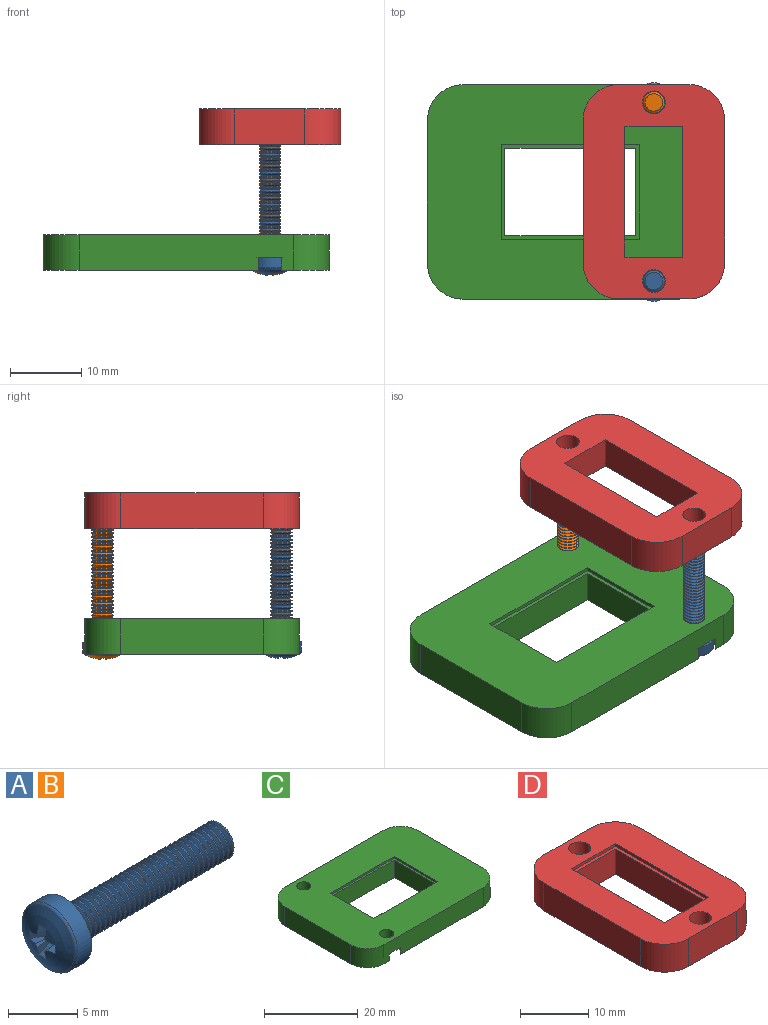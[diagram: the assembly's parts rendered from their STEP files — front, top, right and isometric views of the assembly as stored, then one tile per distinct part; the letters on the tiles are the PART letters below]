
ASSEMBLY  parts=4 mates=3
PART A: 127 faces, bbox 18.4x6.1x6.1 mm
  f0: sphere r=5mm, area 20.9mm2, adj f1,f2,f3,f4,f5,f6,f15,f16
  f1: plane 1.72x0.9mm, normal (0,-1,0), area 0.7mm2, adj f0,f5,f12,f32
  f2: plane 1.72x0.9mm, normal (0,-1,0), area 0.7mm2, adj f0,f6,f9,f33
  f3: plane 1.72x0.9mm, normal (0,1,0), area 0.7mm2, adj f0,f5,f13,f28
  f4: plane 1.72x0.9mm, normal (0,1,0), area 0.7mm2, adj f0,f6,f8,f31
  f5: plane 1.57x0.79mm, normal (-0.45,0,-0.89), area 1.3mm2, adj f0,f1,f3,f12,f13,f26
  f6: plane 1.57x0.79mm, normal (-0.45,0,0.89), area 1.3mm2, adj f0,f2,f4,f8,f9,f27
  f7: plane 0.19x0.11mm, normal (-1,0,0), area 0mm2, adj f16,f17,f34
  f8: plane 0.19x0.11mm, normal (-1,0,0), area 0mm2, adj f4,f6,f34
  f9: plane 0.19x0.11mm, normal (-1,0,0), area 0mm2, adj f2,f6,f34
  f10: plane 0.19x0.11mm, normal (-1,0,0), area 0mm2, adj f18,f20,f34
  f11: plane 0.19x0.11mm, normal (-1,0,0), area 0mm2, adj f18,f19,f34
  f12: plane 0.19x0.11mm, normal (-1,0,0), area 0mm2, adj f1,f5,f34
  f13: plane 0.19x0.11mm, normal (-1,0,0), area 0mm2, adj f3,f5,f34
  f14: plane 0.19x0.11mm, normal (-1,0,0), area 0mm2, adj f15,f17,f34
  f15: plane 1.72x0.9mm, normal (0,0,-1), area 0.7mm2, adj f0,f14,f17,f28
  f16: plane 1.72x0.9mm, normal (0,0,1), area 0.7mm2, adj f0,f7,f17,f31
  f17: plane 1.6x0.81mm, normal (-0.45,0.89,0), area 1.3mm2, adj f0,f7,f14,f15,f16,f29
  f18: plane 1.57x0.79mm, normal (-0.45,-0.89,0), area 1.3mm2, adj f0,f10,f11,f19,f20,f30
  f19: plane 1.72x0.9mm, normal (0,0,-1), area 0.7mm2, adj f0,f11,f18,f32
  f20: plane 1.72x0.9mm, normal (0,0,1), area 0.7mm2, adj f0,f10,f18,f33
  f21: cylinder r=1.5mm len=3mm, axis (-1,0,0), area 6.6mm2, adj f25,f36
  f22: plane 5.6x5.6mm, normal (1,0,0), area 16.6mm2, adj f23,f25
  f23: cylinder r=2.8mm len=5.6mm, axis (-1,0,0), area 24.6mm2, adj f22,f24
  f24: torus R=2.53mm, axis (-1,0,0), area 4.7mm2, adj f0,f23
  f25: torus R=1.6mm, axis (-1,0,0), area 1.5mm2, adj f21,f22
  f26: cone r=0.56mm half-angle=4deg, axis (-1,0,0), area 0mm2, adj f5,f34
  f27: cone r=0.56mm half-angle=4deg, axis (-1,0,0), area 0mm2, adj f6,f34
  f28: cone r=0.56mm half-angle=4deg, axis (-1,0,0), area 0.3mm2, adj f0,f3,f15,f34
  f29: cone r=0.56mm half-angle=4deg, axis (-1,0,0), area 0mm2, adj f17,f34
  f30: cone r=0.56mm half-angle=4deg, axis (-1,0,0), area 0mm2, adj f18,f34
  f31: cone r=0.56mm half-angle=4deg, axis (-1,0,0), area 0.3mm2, adj f0,f4,f16,f34
  f32: cone r=0.56mm half-angle=4deg, axis (-1,0,0), area 0.3mm2, adj f0,f1,f19,f34
  f33: cone r=0.56mm half-angle=4deg, axis (-1,0,0), area 0.3mm2, adj f0,f2,f20,f34
  f34: cone r=0mm half-angle=72deg, axis (-1,0,0), area 1mm2, adj f7,f8,f9,f10,f11,f12,f13,f14
  f35: cone r=1.5mm half-angle=55deg, axis (1,0,0), area 2.9mm2, adj f36,f37
  f36: cone r=1.22mm half-angle=55deg, axis (-1,0,0), area 2.9mm2, adj f21,f35
  f37: cylinder r=1.5mm len=3mm, axis (-1,0,0), area 1mm2, adj f35,f39
  f38: cone r=1.5mm half-angle=55deg, axis (1,0,0), area 2.9mm2, adj f39,f40
  f39: cone r=1.22mm half-angle=55deg, axis (-1,0,0), area 2.9mm2, adj f37,f38
  f40: cylinder r=1.5mm len=3mm, axis (-1,0,0), area 1mm2, adj f38,f42
  f41: cone r=1.5mm half-angle=55deg, axis (1,0,0), area 2.9mm2, adj f42,f43
  f42: cone r=1.22mm half-angle=55deg, axis (-1,0,0), area 2.9mm2, adj f40,f41
  f43: cylinder r=1.5mm len=3mm, axis (-1,0,0), area 1mm2, adj f41,f45
  f44: cone r=1.5mm half-angle=55deg, axis (1,0,0), area 2.9mm2, adj f45,f46
  f45: cone r=1.22mm half-angle=55deg, axis (-1,0,0), area 2.9mm2, adj f43,f44
  f46: cylinder r=1.5mm len=3mm, axis (-1,0,0), area 1mm2, adj f44,f48
  f47: cone r=1.5mm half-angle=55deg, axis (1,0,0), area 2.9mm2, adj f48,f49
  f48: cone r=1.22mm half-angle=55deg, axis (-1,0,0), area 2.9mm2, adj f46,f47
  f49: cylinder r=1.5mm len=3mm, axis (-1,0,0), area 1mm2, adj f47,f51
  f50: cone r=1.5mm half-angle=55deg, axis (1,0,0), area 2.9mm2, adj f51,f52
  f51: cone r=1.22mm half-angle=55deg, axis (-1,0,0), area 2.9mm2, adj f49,f50
  f52: cylinder r=1.5mm len=3mm, axis (-1,0,0), area 1mm2, adj f50,f54
  f53: cone r=1.5mm half-angle=55deg, axis (1,0,0), area 2.9mm2, adj f54,f55
  f54: cone r=1.22mm half-angle=55deg, axis (-1,0,0), area 2.9mm2, adj f52,f53
  f55: cylinder r=1.5mm len=3mm, axis (-1,0,0), area 1mm2, adj f53,f57
  f56: cone r=1.5mm half-angle=55deg, axis (1,0,0), area 2.9mm2, adj f57,f58
  f57: cone r=1.22mm half-angle=55deg, axis (-1,0,0), area 2.9mm2, adj f55,f56
  f58: cylinder r=1.5mm len=3mm, axis (-1,0,0), area 1mm2, adj f56,f60
  f59: cone r=1.5mm half-angle=55deg, axis (1,0,0), area 2.9mm2, adj f60,f61
  f60: cone r=1.22mm half-angle=55deg, axis (-1,0,0), area 2.9mm2, adj f58,f59
  f61: cylinder r=1.5mm len=3mm, axis (-1,0,0), area 1mm2, adj f59,f63
  f62: cone r=1.5mm half-angle=55deg, axis (1,0,0), area 2.9mm2, adj f63,f64
  f63: cone r=1.22mm half-angle=55deg, axis (-1,0,0), area 2.9mm2, adj f61,f62
  f64: cylinder r=1.5mm len=3mm, axis (-1,0,0), area 1mm2, adj f62,f66
  f65: cone r=1.5mm half-angle=55deg, axis (1,0,0), area 2.9mm2, adj f66,f67
  f66: cone r=1.22mm half-angle=55deg, axis (-1,0,0), area 2.9mm2, adj f64,f65
  f67: cylinder r=1.5mm len=3mm, axis (-1,0,0), area 1mm2, adj f65,f69
  f68: cone r=1.5mm half-angle=55deg, axis (1,0,0), area 2.9mm2, adj f69,f70
  f69: cone r=1.22mm half-angle=55deg, axis (-1,0,0), area 2.9mm2, adj f67,f68
  f70: cylinder r=1.5mm len=3mm, axis (-1,0,0), area 1mm2, adj f68,f72
  f71: cone r=1.5mm half-angle=55deg, axis (1,0,0), area 2.9mm2, adj f72,f73
  f72: cone r=1.22mm half-angle=55deg, axis (-1,0,0), area 2.9mm2, adj f70,f71
  f73: cylinder r=1.5mm len=3mm, axis (-1,0,0), area 1mm2, adj f71,f75
  f74: cone r=1.5mm half-angle=55deg, axis (1,0,0), area 2.9mm2, adj f75,f76
  f75: cone r=1.22mm half-angle=55deg, axis (-1,0,0), area 2.9mm2, adj f73,f74
  f76: cylinder r=1.5mm len=3mm, axis (-1,0,0), area 1mm2, adj f74,f78
  f77: cone r=1.5mm half-angle=55deg, axis (1,0,0), area 2.9mm2, adj f78,f79
  f78: cone r=1.22mm half-angle=55deg, axis (-1,0,0), area 2.9mm2, adj f76,f77
  f79: cylinder r=1.5mm len=3mm, axis (-1,0,0), area 1mm2, adj f77,f81
  f80: cone r=1.5mm half-angle=55deg, axis (1,0,0), area 2.9mm2, adj f81,f82
  f81: cone r=1.22mm half-angle=55deg, axis (-1,0,0), area 2.9mm2, adj f79,f80
  f82: cylinder r=1.5mm len=3mm, axis (-1,0,0), area 1mm2, adj f80,f84
  f83: cone r=1.5mm half-angle=55deg, axis (1,0,0), area 2.9mm2, adj f84,f85
  f84: cone r=1.22mm half-angle=55deg, axis (-1,0,0), area 2.9mm2, adj f82,f83
  f85: cylinder r=1.5mm len=3mm, axis (-1,0,0), area 1mm2, adj f83,f87
  f86: cone r=1.5mm half-angle=55deg, axis (1,0,0), area 2.9mm2, adj f87,f88
  f87: cone r=1.22mm half-angle=55deg, axis (-1,0,0), area 2.9mm2, adj f85,f86
  f88: cylinder r=1.5mm len=3mm, axis (-1,0,0), area 1mm2, adj f86,f90
  f89: cone r=1.5mm half-angle=55deg, axis (1,0,0), area 2.9mm2, adj f90,f91
  f90: cone r=1.22mm half-angle=55deg, axis (-1,0,0), area 2.9mm2, adj f88,f89
  f91: cylinder r=1.5mm len=3mm, axis (-1,0,0), area 1mm2, adj f89,f93
  f92: cone r=1.5mm half-angle=55deg, axis (1,0,0), area 2.9mm2, adj f93,f94
  f93: cone r=1.22mm half-angle=55deg, axis (-1,0,0), area 2.9mm2, adj f91,f92
  f94: cylinder r=1.5mm len=3mm, axis (-1,0,0), area 1mm2, adj f92,f96
  f95: cone r=1.5mm half-angle=55deg, axis (1,0,0), area 2.9mm2, adj f96,f97
  f96: cone r=1.22mm half-angle=55deg, axis (-1,0,0), area 2.9mm2, adj f94,f95
  f97: cylinder r=1.5mm len=3mm, axis (-1,0,0), area 1mm2, adj f95,f99
  f98: cone r=1.5mm half-angle=55deg, axis (1,0,0), area 2.9mm2, adj f99,f100
  f99: cone r=1.22mm half-angle=55deg, axis (-1,0,0), area 2.9mm2, adj f97,f98
  f100: cylinder r=1.5mm len=3mm, axis (-1,0,0), area 1mm2, adj f98,f102
  f101: cone r=1.5mm half-angle=55deg, axis (1,0,0), area 2.9mm2, adj f102,f103
  f102: cone r=1.22mm half-angle=55deg, axis (-1,0,0), area 2.9mm2, adj f100,f101
  f103: cylinder r=1.5mm len=3mm, axis (-1,0,0), area 1mm2, adj f101,f105
  f104: cone r=1.5mm half-angle=55deg, axis (1,0,0), area 2.9mm2, adj f105,f106
  f105: cone r=1.22mm half-angle=55deg, axis (-1,0,0), area 2.9mm2, adj f103,f104
  f106: cylinder r=1.5mm len=3mm, axis (-1,0,0), area 1mm2, adj f104,f108
  f107: cone r=1.5mm half-angle=55deg, axis (1,0,0), area 2.9mm2, adj f108,f109
  f108: cone r=1.22mm half-angle=55deg, axis (-1,0,0), area 2.9mm2, adj f106,f107
  f109: cylinder r=1.5mm len=3mm, axis (-1,0,0), area 1mm2, adj f107,f111
  f110: cone r=1.5mm half-angle=55deg, axis (1,0,0), area 2.9mm2, adj f111,f112
  f111: cone r=1.22mm half-angle=55deg, axis (-1,0,0), area 2.9mm2, adj f109,f110
  f112: cylinder r=1.5mm len=3mm, axis (-1,0,0), area 1mm2, adj f110,f114
  f113: cone r=1.5mm half-angle=55deg, axis (1,0,0), area 2.9mm2, adj f114,f115
  f114: cone r=1.22mm half-angle=55deg, axis (-1,0,0), area 2.9mm2, adj f112,f113
  f115: cylinder r=1.5mm len=3mm, axis (-1,0,0), area 1mm2, adj f113,f117
  f116: cone r=1.5mm half-angle=55deg, axis (1,0,0), area 2.9mm2, adj f117,f118
  f117: cone r=1.22mm half-angle=55deg, axis (-1,0,0), area 2.9mm2, adj f115,f116
  f118: cylinder r=1.5mm len=3mm, axis (-1,0,0), area 1mm2, adj f116,f120
  f119: cone r=1.5mm half-angle=55deg, axis (1,0,0), area 2.9mm2, adj f120,f121
  f120: cone r=1.22mm half-angle=55deg, axis (-1,0,0), area 2.9mm2, adj f118,f119
  f121: cylinder r=1.5mm len=3mm, axis (-1,0,0), area 1mm2, adj f119,f123
  f122: cone r=1.5mm half-angle=55deg, axis (1,0,0), area 2.9mm2, adj f123,f124
  f123: cone r=1.22mm half-angle=55deg, axis (-1,0,0), area 2.9mm2, adj f121,f122
  f124: cylinder r=1.5mm len=3mm, axis (-1,0,0), area 1mm2, adj f122,f125
  f125: cone r=1.22mm half-angle=55deg, axis (-1,0,0), area 2.9mm2, adj f124,f126
  f126: plane 2.44x2.44mm, normal (1,0,0), area 4.7mm2, adj f125
PART B: same geometry as A
PART C: 25 faces, bbox 40x30x5 mm
  f0: plane 30x5mm, normal (0,1,0), area 144mm2, adj f8,f9,f16,f18,f23,f24
  f1: plane 30x5mm, normal (0,-1,0), area 144mm2, adj f8,f9,f15,f17,f19,f20
  f2: plane 13.2x0.5mm, normal (1,0,0), area 6.6mm2, adj f3,f7,f8,f14
  f3: plane 19.3x0.5mm, normal (0,-1,0), area 9.7mm2, adj f2,f4,f8,f14
  f4: plane 13.2x0.5mm, normal (-1,0,0), area 6.6mm2, adj f3,f7,f8,f14
  f5: plane 20x5mm, normal (-1,0,0), area 100mm2, adj f8,f9,f17,f18
  f6: plane 20x5mm, normal (1,0,0), area 100mm2, adj f8,f9,f15,f16
  f7: plane 19.3x0.5mm, normal (0,1,0), area 9.7mm2, adj f2,f4,f8,f14
  f8: plane 40x30mm, normal (0,0,1), area 909.6mm2, adj f0,f1,f2,f3,f4,f5,f6,f7
  f9: plane 40x30mm, normal (0,0,-1), area 901mm2, adj f0,f1,f5,f6,f10,f11,f12,f13
  f10: plane 18.3x4.5mm, normal (0,-1,0), area 82.3mm2, adj f9,f11,f13,f14
  f11: plane 12.2x4.5mm, normal (-1,0,0), area 54.9mm2, adj f9,f10,f12,f14
  f12: plane 18.3x4.5mm, normal (0,1,0), area 82.3mm2, adj f9,f11,f13,f14
  f13: plane 12.2x4.5mm, normal (1,0,0), area 54.9mm2, adj f9,f10,f12,f14
  f14: plane 19.3x13.2mm, normal (0,0,1), area 31.5mm2, adj f2,f3,f4,f7,f10,f11,f12,f13
  f15: cylinder r=5mm len=5mm, axis (0,0,-1), area 39.3mm2, adj f1,f6,f8,f9
  f16: cylinder r=5mm len=5mm, axis (0,0,1), area 39.3mm2, adj f0,f6,f8,f9
  f17: cylinder r=5mm len=5mm, axis (0,0,1), area 39.3mm2, adj f1,f5,f8,f9
  f18: cylinder r=5mm len=5mm, axis (0,0,-1), area 39.3mm2, adj f0,f5,f8,f9
  f19: plane 6x5.5mm, normal (0,0,-1), area 20.1mm2, adj f1,f20,f21
  f20: cylinder r=3mm len=6mm, axis (0,0,-1), area 27.6mm2, adj f1,f9,f19
  f21: cylinder r=1.5mm len=3.2mm, axis (0,0,-1), area 30.2mm2, adj f8,f19
  f22: cylinder r=1.5mm len=3.2mm, axis (0,0,-1), area 30.2mm2, adj f8,f23
  f23: plane 6x5.5mm, normal (0,0,-1), area 20.1mm2, adj f0,f22,f24
  f24: cylinder r=3mm len=6mm, axis (0,0,-1), area 27.6mm2, adj f0,f9,f23
PART D: 21 faces, bbox 19.8x30x5 mm
  f0: plane 9.8x5mm, normal (0,1,0), area 49mm2, adj f8,f9,f15,f18
  f1: plane 20x5mm, normal (-1,0,0), area 100mm2, adj f8,f9,f15,f16
  f2: plane 9.8x5mm, normal (0,-1,0), area 49mm2, adj f8,f9,f16,f17
  f3: plane 9.1x0.5mm, normal (0,1,0), area 4.6mm2, adj f4,f6,f8,f14
  f4: plane 19.3x0.5mm, normal (1,0,0), area 9.7mm2, adj f3,f5,f8,f14
  f5: plane 9.1x0.5mm, normal (0,-1,0), area 4.6mm2, adj f4,f6,f8,f14
  f6: plane 19.3x0.5mm, normal (-1,0,0), area 9.7mm2, adj f3,f5,f8,f14
  f7: plane 20x5mm, normal (1,0,0), area 100mm2, adj f8,f9,f17,f18
  f8: plane 30x19.8mm, normal (0,0,1), area 380.8mm2, adj f0,f1,f2,f3,f4,f5,f6,f7
  f9: plane 30x19.8mm, normal (0,0,-1), area 408.2mm2, adj f0,f1,f2,f7,f10,f11,f12,f13
  f10: plane 18.3x4.5mm, normal (-1,0,0), area 82.4mm2, adj f9,f11,f13,f14
  f11: plane 8.1x4.5mm, normal (0,1,0), area 36.4mm2, adj f9,f10,f12,f14
  f12: plane 18.3x4.5mm, normal (1,0,0), area 82.4mm2, adj f9,f11,f13,f14
  f13: plane 8.1x4.5mm, normal (0,-1,0), area 36.4mm2, adj f9,f10,f12,f14
  f14: plane 19.3x9.1mm, normal (0,0,1), area 27.4mm2, adj f3,f4,f5,f6,f10,f11,f12,f13
  f15: cylinder r=5mm len=5mm, axis (0,0,-1), area 39.3mm2, adj f0,f1,f8,f9
  f16: cylinder r=5mm len=5mm, axis (0,0,1), area 39.3mm2, adj f1,f2,f8,f9
  f17: cylinder r=5mm len=5mm, axis (0,0,-1), area 39.3mm2, adj f2,f7,f8,f9
  f18: cylinder r=5mm len=5mm, axis (0,0,1), area 39.3mm2, adj f0,f7,f8,f9
  f19: cylinder r=1.6mm len=5mm, axis (0,0,-1), area 50.3mm2, adj f8,f9
  f20: cylinder r=1.6mm len=5mm, axis (0,0,-1), area 50.3mm2, adj f8,f9
PLACE A rot(axis=(0,-1,0),90deg) t=(-4.59,1.49,1.34)mm
PLACE B rot(axis=(0,-1,0),90deg) t=(-4.59,26.49,1.24)mm
PLACE C rot(axis=(0,0,1),180deg) t=(-16.29,13.99,1.94)mm fixed
PLACE D rot(axis=(1,0,0),180deg) t=(7.11,13.99,44.54)mm
MATE slider D.f20 <-> A.f125  axis (0,0,-1) through (-4.59,1.49,19.54)mm
MATE fastened C.f20 <-> B.f21  axis (0,0,-1) through (-4.59,26.49,3.74)mm
MATE fastened C.f22 <-> A.f21  axis (0,0,-1) through (-4.59,1.49,3.74)mm
